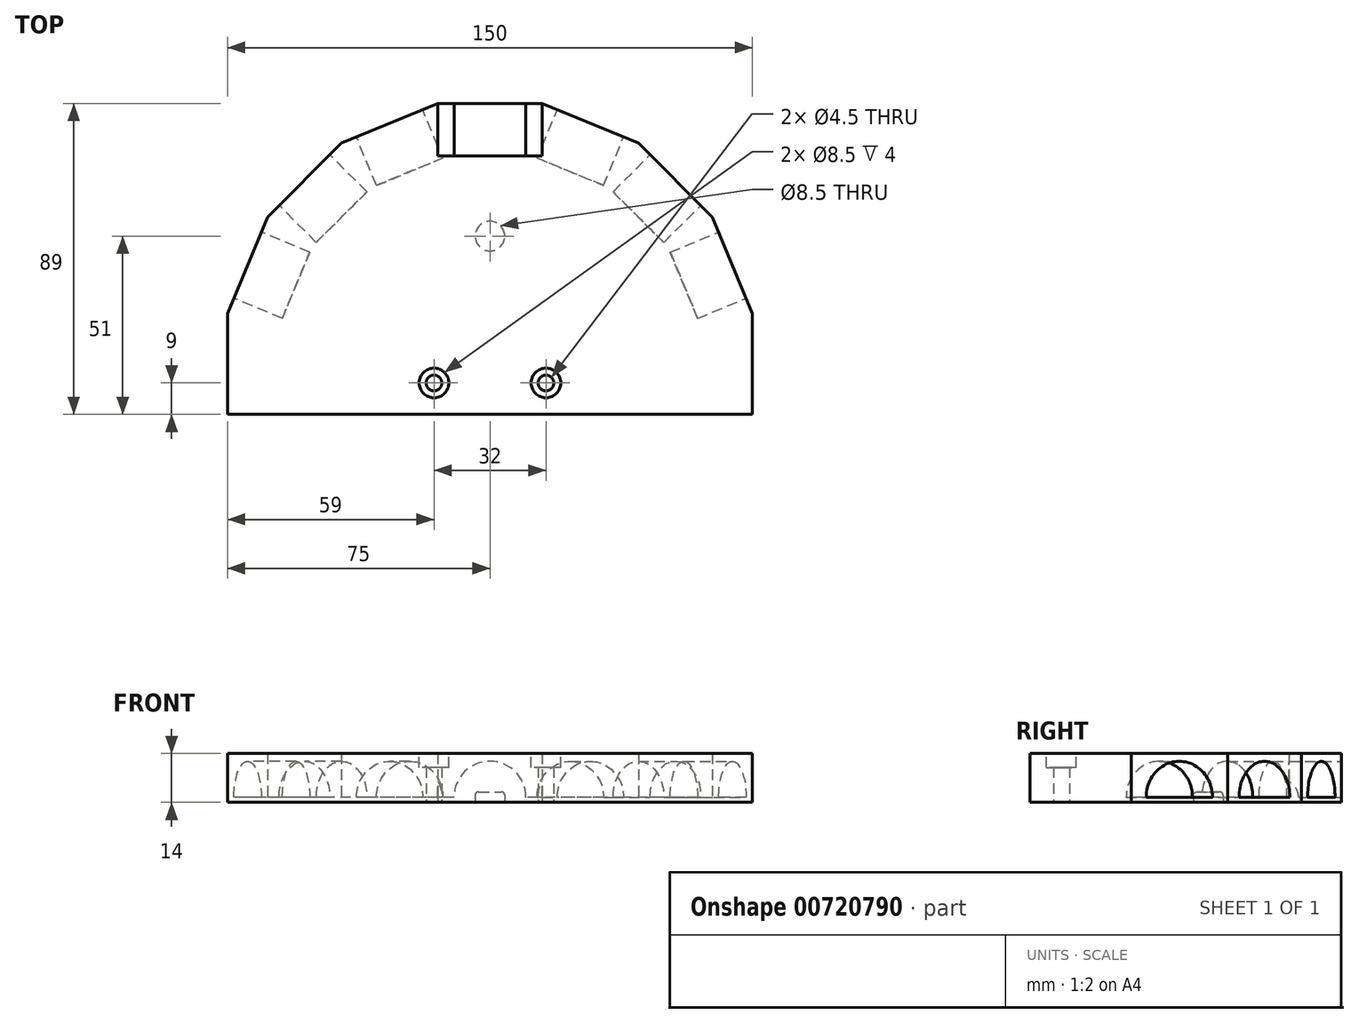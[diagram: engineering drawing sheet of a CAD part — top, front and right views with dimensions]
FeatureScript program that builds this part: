
annotation { "Feature Type Name" : "Feature", "Feature Type Description" : "" }
export const myFeature = defineFeature(function(context is Context, id is Id, definition is map)
    precondition{}
    {
        {
            var Q0;
            Q0=qCreatedBy(makeId("Top.planeOp"),FACE);
            var sketch = newSketch(context, id + "F0", { "sketchPlane" : qUnion([Q0])});
            skLineSegment(sketch, "E0.bottom", {"start": v(0, 0) * mm, "end": v(150, 0) * mm});
            skLineSegment(sketch, "E0.top", {"start": v(0, -10) * mm, "end": v(150, -10) * mm});
            skLineSegment(sketch, "E0.left", {"start": v(0, 0) * mm, "end": v(0, -10) * mm});
            skLineSegment(sketch, "E0.right", {"start": v(150, 0) * mm, "end": v(150, -10) * mm});
            skLineSegment(sketch, "E1", {"start": v(75, 0) * mm, "end": v(75, -10) * mm, "construction": true});
            skLineSegment(sketch, "E2", {"start": v(75, -5) * mm, "end": v(91, -5) * mm, "construction": true});
            skLineSegment(sketch, "E3", {"start": v(91, -5) * mm, "end": v(59, -5) * mm, "construction": true});
            skCircle(sketch, "E4", {"center": v(59, -5) * mm, "radius": 2.25 * mm});
            skCircle(sketch, "E5", {"center": v(91, -5) * mm, "radius": 2.25 * mm});
            skCircle(sketch, "E6.cCircle", {"center": v(75, 0) * mm, "radius": 75 * mm, "construction": true});
            skLineSegment(sketch, "E6.0", {"start": v(150, 14.92) * mm, "end": v(150, -14.92) * mm});
            skLineSegment(sketch, "E6.1", {"start": v(150, -14.92) * mm, "end": v(138.58, -42.48) * mm});
            skLineSegment(sketch, "E6.2", {"start": v(138.58, -42.48) * mm, "end": v(117.48, -63.58) * mm});
            skLineSegment(sketch, "E6.3", {"start": v(117.48, -63.58) * mm, "end": v(89.92, -75) * mm});
            skLineSegment(sketch, "E6.4", {"start": v(89.92, -75) * mm, "end": v(60.08, -75) * mm});
            skLineSegment(sketch, "E6.5", {"start": v(60.08, -75) * mm, "end": v(32.52, -63.58) * mm});
            skLineSegment(sketch, "E6.6", {"start": v(32.52, -63.58) * mm, "end": v(11.42, -42.48) * mm});
            skLineSegment(sketch, "E6.7", {"start": v(11.42, -42.48) * mm, "end": v(0, -14.92) * mm});
            skLineSegment(sketch, "E6.8", {"start": v(0, -14.92) * mm, "end": v(0, 14.92) * mm});
            skLineSegment(sketch, "E6.9", {"start": v(0, 14.92) * mm, "end": v(11.42, 42.48) * mm});
            skLineSegment(sketch, "E6.10", {"start": v(11.42, 42.48) * mm, "end": v(32.52, 63.58) * mm});
            skLineSegment(sketch, "E6.11", {"start": v(32.52, 63.58) * mm, "end": v(60.08, 75) * mm});
            skLineSegment(sketch, "E6.12", {"start": v(60.08, 75) * mm, "end": v(89.92, 75) * mm});
            skLineSegment(sketch, "E6.13", {"start": v(89.92, 75) * mm, "end": v(117.48, 63.58) * mm});
            skLineSegment(sketch, "E6.14", {"start": v(117.48, 63.58) * mm, "end": v(138.58, 42.48) * mm});
            skLineSegment(sketch, "E6.15", {"start": v(138.58, 42.48) * mm, "end": v(150, 14.92) * mm});
            skPoint(sketch, "E6.0.midPoint", {"position": v(150, 0) * mm});
            skSolve(sketch);
        }
        {
            var Q0;
            {var subQ2=sQuery(id+"F0.wireOp",EDGE,"E0.bottom");Q0=makeQuery(id+"F0.imprint","IMPRINT",FACE,{"disambiguationData":[TD([[makeQuery(id+"F0.imprint","IMPRINT",EDGE,{"derivedFrom":subQ2}),1.0]])]});}
            var Q1;
            {var subQ7=sQuery(id+"F0.wireOp",EDGE,"E0.bottom");Q1=makeQuery(id+"F0.imprint","IMPRINT",FACE,{"disambiguationData":[TD([[makeQuery(id+"F0.imprint","IMPRINT",EDGE,{"derivedFrom":subQ7}),-1.0]])]});}
            var Q2;
            {var subQ0=sQuery(id+"F0.wireOp",EDGE,"E0.left");Q2=makeQuery(id+"F0.imprint","IMPRINT",FACE,{"disambiguationData":[TD([[makeQuery(id+"F0.imprint","IMPRINT",EDGE,{"derivedFrom":subQ0}),1.0]])]});}
            var Q3;
            {var subQ0=sQuery(id+"F0.wireOp",EDGE,"E0.right");Q3=makeQuery(id+"F0.imprint","IMPRINT",FACE,{"disambiguationData":[TD([[makeQuery(id+"F0.imprint","IMPRINT",EDGE,{"derivedFrom":subQ0}),-1.0]])]});}
            extrude(context, id + "F1", {"entities" : qUnion([Q0, Q1, Q2, Q3]), "depth" : 14 * mm, "offsetDistance" : 25 * mm});
        }
        {
            var Q0;
            Q0=makeQuery(id+"F1.opExtrude","SWEPT_FACE",FACE,{"disambiguationData":[OSD([sQuery(id+"F0.wireOp",EDGE,"E6.12")])]});
            var sketch = newSketch(context, id + "F2", { "sketchPlane" : qUnion([Q0])});
            skLineSegment(sketch, "E7", {"start": v(-89.92, 0) * mm, "end": v(-89.92, 1.5) * mm, "construction": true});
            skLineSegment(sketch, "E8", {"start": v(-89.92, 1.5) * mm, "end": v(-60.08, 1.5) * mm});
            skArc(sketch, "E9", {"start": v(-85.25, 1.5) * mm, "mid": v(-75, 11.75) * mm, "end": v(-64.75, 1.5) * mm});
            skSolve(sketch);
        }
        {
            var Q0;
            Q0=makeQuery(id+"F1.opExtrude","SWEPT_FACE",FACE,{"disambiguationData":[OSD([sQuery(id+"F0.wireOp",EDGE,"E6.10")])]});
            var sketch = newSketch(context, id + "F3", { "sketchPlane" : qUnion([Q0])});
            skLineSegment(sketch, "E10", {"start": v(-67.95, 0) * mm, "end": v(-67.95, 1.5) * mm});
            skLineSegment(sketch, "E11", {"start": v(-67.95, 1.5) * mm, "end": v(-38.11, 1.5) * mm});
            skArc(sketch, "E12", {"start": v(-42.78, 1.5) * mm, "mid": v(-53.03, 11.75) * mm, "end": v(-63.28, 1.5) * mm});
            skSolve(sketch);
        }
        {
            var Q0;
            Q0=makeQuery(id+"F1.opExtrude","SWEPT_FACE",FACE,{"disambiguationData":[OSD([sQuery(id+"F0.wireOp",EDGE,"E6.14")])]});
            var sketch = newSketch(context, id + "F4", { "sketchPlane" : qUnion([Q0])});
            skLineSegment(sketch, "E13", {"start": v(-67.95, 0) * mm, "end": v(-67.95, 1.5) * mm});
            skLineSegment(sketch, "E14", {"start": v(-67.95, 1.5) * mm, "end": v(-38.11, 1.5) * mm});
            skArc(sketch, "E15", {"start": v(-42.78, 1.5) * mm, "mid": v(-53.03, 11.75) * mm, "end": v(-63.28, 1.5) * mm});
            skSolve(sketch);
        }
        {
            var Q0;
            Q0 = qSketchRegion(id + "F4", true);
            extrude(context, id + "F5", {"entities" : qUnion([Q0]), "operationType" : NewBodyOperationType.REMOVE, "oppositeDirection" : true, "depth" : 15 * mm, "offsetDistance" : 25 * mm});
        }
        {
            var Q0;
            {var subQ0=sQuery(id+"F2.wireOp",EDGE,"E9");Q0=makeQuery(id+"F2.imprint","IMPRINT",FACE,{"disambiguationData":[TD([[makeQuery(id+"F2.imprint","IMPRINT",EDGE,{"derivedFrom":subQ0}),-1.0]])]});}
            extrude(context, id + "F6", {"entities" : qUnion([Q0]), "operationType" : NewBodyOperationType.REMOVE, "oppositeDirection" : true, "depth" : 15 * mm, "offsetDistance" : 25 * mm});
        }
        {
            var Q0;
            {var subQ0=sQuery(id+"F3.wireOp",EDGE,"E12");Q0=makeQuery(id+"F3.imprint","IMPRINT",FACE,{"disambiguationData":[TD([[makeQuery(id+"F3.imprint","IMPRINT",EDGE,{"derivedFrom":subQ0}),1.0]])]});}
            extrude(context, id + "F7", {"entities" : qUnion([Q0]), "operationType" : NewBodyOperationType.REMOVE, "oppositeDirection" : true, "depth" : 15 * mm, "offsetDistance" : 25 * mm});
        }
        {
            var Q0;
            Q0=makeQuery(id+"F1.opExtrude","CAP_FACE",FACE,{"disambiguationData":[OSD([sQuery(id+"F0.wireOp",EDGE,"E0.top"),sQuery(id+"F0.wireOp",EDGE,"E0.left"),sQuery(id+"F0.wireOp",EDGE,"E0.right"),sQuery(id+"F0.wireOp",EDGE,"E4"),sQuery(id+"F0.wireOp",EDGE,"E5"),sQuery(id+"F0.wireOp",EDGE,"E6.0"),sQuery(id+"F0.wireOp",EDGE,"E6.8"),sQuery(id+"F0.wireOp",EDGE,"E6.9"),sQuery(id+"F0.wireOp",EDGE,"E6.10"),sQuery(id+"F0.wireOp",EDGE,"E6.11"),sQuery(id+"F0.wireOp",EDGE,"E6.12"),sQuery(id+"F0.wireOp",EDGE,"E6.13"),sQuery(id+"F0.wireOp",EDGE,"E6.14"),sQuery(id+"F0.wireOp",EDGE,"E6.15")])],"isStart":false});
            var sketch = newSketch(context, id + "F8", { "sketchPlane" : qUnion([Q0])});
            skCircle(sketch, "E16", {"center": v(59, -5) * mm, "radius": 4.25 * mm});
            skCircle(sketch, "E17", {"center": v(91, -5) * mm, "radius": 4.25 * mm});
            skSolve(sketch);
        }
        {
            var Q0;
            Q0 = qSketchRegion(id + "F8", true);
            extrude(context, id + "F9", {"entities" : qUnion([Q0]), "operationType" : NewBodyOperationType.REMOVE, "oppositeDirection" : true, "depth" : 4 * mm, "offsetDistance" : 25 * mm});
        }
        {
            var Q0;
            Q0=makeQuery(id+"F1.opExtrude","SWEPT_FACE",FACE,{"disambiguationData":[OSD([sQuery(id+"F0.wireOp",EDGE,"E0.top")])]});
            var sketch = newSketch(context, id + "F10", { "sketchPlane" : qUnion([Q0])});
            skSolve(sketch);
        }
        {
            var Q0;
            Q0 = qSketchRegion(id + "F10", true);
            var Q1;
            {var subQ0=sQuery(id+"F0.wireOp",EDGE,"E0.top");Q1=makeQuery(id+"F10.imprint","IMPRINT",FACE,{"disambiguationData":[TD([[makeQuery(id+"F10.imprint","IMPRINT",EDGE,{"derivedFrom":makeQuery(id+"F1.opExtrude","CAP_EDGE",EDGE,{"disambiguationData":[OSD([subQ0])],"isStart":true})}),1.0]])]});}
            extrude(context, id + "F11", {"entities" : qUnion([Q0, Q1]), "operationType" : NewBodyOperationType.ADD, "depth" : 4 * mm, "offsetDistance" : 25 * mm});
        }
        {
            var Q0;
            {var subQ0=sQuery(id+"F0.wireOp",EDGE,"E0.top");Q0=makeQuery(id+"F11.boolean.opBoolean","MERGE",FACE,{"derivedFrom":[makeQuery(id+"F1.opExtrude","CAP_FACE",FACE,{"disambiguationData":[OSD([subQ0,sQuery(id+"F0.wireOp",EDGE,"E0.left"),sQuery(id+"F0.wireOp",EDGE,"E0.right"),sQuery(id+"F0.wireOp",EDGE,"E4"),sQuery(id+"F0.wireOp",EDGE,"E5"),sQuery(id+"F0.wireOp",EDGE,"E6.0"),sQuery(id+"F0.wireOp",EDGE,"E6.8"),sQuery(id+"F0.wireOp",EDGE,"E6.9"),sQuery(id+"F0.wireOp",EDGE,"E6.10"),sQuery(id+"F0.wireOp",EDGE,"E6.11"),sQuery(id+"F0.wireOp",EDGE,"E6.12"),sQuery(id+"F0.wireOp",EDGE,"E6.13"),sQuery(id+"F0.wireOp",EDGE,"E6.14"),sQuery(id+"F0.wireOp",EDGE,"E6.15")])],"isStart":true}),makeQuery(id+"F11.opExtrude","SWEPT_FACE",FACE,{"disambiguationData":[OSD([subQ0]),TDD([makeQuery(id+"F10.imprint","IMPRINT",EDGE,{"derivedFrom":makeQuery(id+"F1.opExtrude","CAP_EDGE",EDGE,{"disambiguationData":[OSD([subQ0])],"isStart":true})})])]})]});}
            var sketch = newSketch(context, id + "F12", { "sketchPlane" : qUnion([Q0])});
            skLineSegment(sketch, "E18", {"start": v(91, 5) * mm, "end": v(59, 5) * mm, "construction": true});
            skLineSegment(sketch, "E19", {"start": v(75, 5) * mm, "end": v(75, -37) * mm, "construction": true});
            skCircle(sketch, "E20", {"center": v(75, -37) * mm, "radius": 4.25 * mm});
            skSolve(sketch);
        }
        {
            var Q0;
            {var subQ0=sQuery(id+"F12.wireOp",EDGE,"E20");var subQ1=makeQuery(id+"F1.opExtrude","CAP_EDGE",EDGE,{"disambiguationData":[OSD([sQuery(id+"F0.wireOp",EDGE,"E6.12")])],"isStart":true});var subQ2=makeQuery(id+"F12.imprint","INTERSECT",VERTEX,{"disambiguationData":[OD(0.0)],"derivedFrom":[subQ1,subQ0]});Q0=makeQuery(id+"F12.imprint","IMPRINT",FACE,{"disambiguationData":[TD([[makeQuery(id+"F12.imprint","IMPRINT",EDGE,{"disambiguationData":[TD([[subQ2,-1.0]])],"derivedFrom":subQ0}),1.0]])]});}
            var Q1;
            {var subQ0=sQuery(id+"F12.wireOp",EDGE,"E20");var subQ1=makeQuery(id+"F1.opExtrude","CAP_EDGE",EDGE,{"disambiguationData":[OSD([sQuery(id+"F0.wireOp",EDGE,"E6.12")])],"isStart":true});var subQ2=makeQuery(id+"F12.imprint","INTERSECT",VERTEX,{"disambiguationData":[OD(0.0)],"derivedFrom":[subQ1,subQ0]});Q1=makeQuery(id+"F12.imprint","IMPRINT",FACE,{"disambiguationData":[TD([[makeQuery(id+"F12.imprint","IMPRINT",EDGE,{"disambiguationData":[TD([[subQ2,1.0]])],"derivedFrom":subQ0}),1.0]])]});}
            extrude(context, id + "F13", {"entities" : qUnion([Q0, Q1]), "operationType" : NewBodyOperationType.REMOVE, "oppositeDirection" : true, "depth" : 3 * mm, "offsetDistance" : 25 * mm});
        }
        {
            var Q0;
            Q0=makeQuery(id+"F13.boolean.opBoolean","COPY",EDGE,{"derivedFrom":makeQuery(id+"F13.opExtrude","CAP_EDGE",EDGE,{"disambiguationData":[OSD([sQuery(id+"F12.wireOp",EDGE,"E20")])],"isStart":true})});
            var Q1;
            Q1=makeQuery(id+"F13.boolean.opBoolean","COPY",EDGE,{"derivedFrom":makeQuery(id+"F13.opExtrude","CAP_EDGE",EDGE,{"disambiguationData":[OSD([sQuery(id+"F12.wireOp",EDGE,"E20")])],"isStart":false})});
            fillet(context, id + "F14", {"entities" : qUnion([Q0, Q1]), "radius" : 1 * mm, "tangentPropagation" : true, "allowEdgeOverflow" : false});
        }
        {
            var Q0;
            Q0=makeQuery(id+"F1.opExtrude","SWEPT_FACE",FACE,{"disambiguationData":[OSD([sQuery(id+"F0.wireOp",EDGE,"E6.9")])]});
            var sketch = newSketch(context, id + "F15", { "sketchPlane" : qUnion([Q0])});
            skLineSegment(sketch, "E21", {"start": v(-43.62, 0) * mm, "end": v(-43.62, 1.5) * mm, "construction": true});
            skLineSegment(sketch, "E22", {"start": v(-43.62, 1.5) * mm, "end": v(-13.78, 1.5) * mm});
            skArc(sketch, "E23", {"start": v(-18.45, 1.5) * mm, "mid": v(-28.7, 11.75) * mm, "end": v(-38.95, 1.5) * mm});
            skSolve(sketch);
        }
        {
            var Q0;
            Q0=makeQuery(id+"F1.opExtrude","SWEPT_FACE",FACE,{"disambiguationData":[OSD([sQuery(id+"F0.wireOp",EDGE,"E6.15")])]});
            var sketch = newSketch(context, id + "F16", { "sketchPlane" : qUnion([Q0])});
            skLineSegment(sketch, "E24", {"start": v(-43.62, 0) * mm, "end": v(-43.62, 1.5) * mm, "construction": true});
            skLineSegment(sketch, "E25", {"start": v(-43.62, 1.5) * mm, "end": v(-13.78, 1.5) * mm});
            skArc(sketch, "E26", {"start": v(-18.45, 1.5) * mm, "mid": v(-28.7, 11.75) * mm, "end": v(-38.95, 1.5) * mm});
            skSolve(sketch);
        }
        {
            var Q0;
            Q0 = qSketchRegion(id + "F16", true);
            extrude(context, id + "F17", {"entities" : qUnion([Q0]), "operationType" : NewBodyOperationType.REMOVE, "oppositeDirection" : true, "depth" : 15 * mm, "offsetDistance" : 25 * mm});
        }
        {
            var Q0;
            {var subQ0=sQuery(id+"F15.wireOp",EDGE,"E23");Q0=makeQuery(id+"F15.imprint","IMPRINT",FACE,{"disambiguationData":[TD([[makeQuery(id+"F15.imprint","IMPRINT",EDGE,{"derivedFrom":subQ0}),1.0]])]});}
            extrude(context, id + "F18", {"entities" : qUnion([Q0]), "operationType" : NewBodyOperationType.REMOVE, "oppositeDirection" : true, "depth" : 15 * mm, "offsetDistance" : 25 * mm});
        }
        {
            var Q0;
            Q0=makeQuery(id+"F1.opExtrude","SWEPT_FACE",FACE,{"disambiguationData":[OSD([sQuery(id+"F0.wireOp",EDGE,"E6.13")])]});
            var sketch = newSketch(context, id + "F19", { "sketchPlane" : qUnion([Q0])});
            skLineSegment(sketch, "E27", {"start": v(-84.2, 0) * mm, "end": v(-84.2, 1.5) * mm});
            skLineSegment(sketch, "E28", {"start": v(-84.2, 1.5) * mm, "end": v(-54.37, 1.5) * mm});
            skArc(sketch, "E29", {"start": v(-59.04, 1.5) * mm, "mid": v(-69.3, 11.75) * mm, "end": v(-79.54, 1.5) * mm});
            skSolve(sketch);
        }
        {
            var Q0;
            Q0=makeQuery(id+"F1.opExtrude","SWEPT_FACE",FACE,{"disambiguationData":[OSD([sQuery(id+"F0.wireOp",EDGE,"E6.11")])]});
            var sketch = newSketch(context, id + "F20", { "sketchPlane" : qUnion([Q0])});
            skLineSegment(sketch, "E30", {"start": v(-84.2, 0) * mm, "end": v(-84.2, 1.5) * mm});
            skLineSegment(sketch, "E31", {"start": v(-84.2, 1.5) * mm, "end": v(-54.37, 1.5) * mm});
            skArc(sketch, "E32", {"start": v(-59.04, 1.5) * mm, "mid": v(-69.3, 11.75) * mm, "end": v(-79.54, 1.5) * mm});
            skSolve(sketch);
        }
        {
            var Q0;
            Q0 = qSketchRegion(id + "F20", true);
            extrude(context, id + "F21", {"entities" : qUnion([Q0]), "operationType" : NewBodyOperationType.REMOVE, "oppositeDirection" : true, "depth" : 15 * mm, "offsetDistance" : 25 * mm});
        }
        {
            var Q0;
            {var subQ0=sQuery(id+"F19.wireOp",EDGE,"E29");Q0=makeQuery(id+"F19.imprint","IMPRINT",FACE,{"disambiguationData":[TD([[makeQuery(id+"F19.imprint","IMPRINT",EDGE,{"derivedFrom":subQ0}),1.0]])]});}
            extrude(context, id + "F22", {"entities" : qUnion([Q0]), "operationType" : NewBodyOperationType.REMOVE, "oppositeDirection" : true, "depth" : 15 * mm, "offsetDistance" : 25 * mm});
        }
    });
